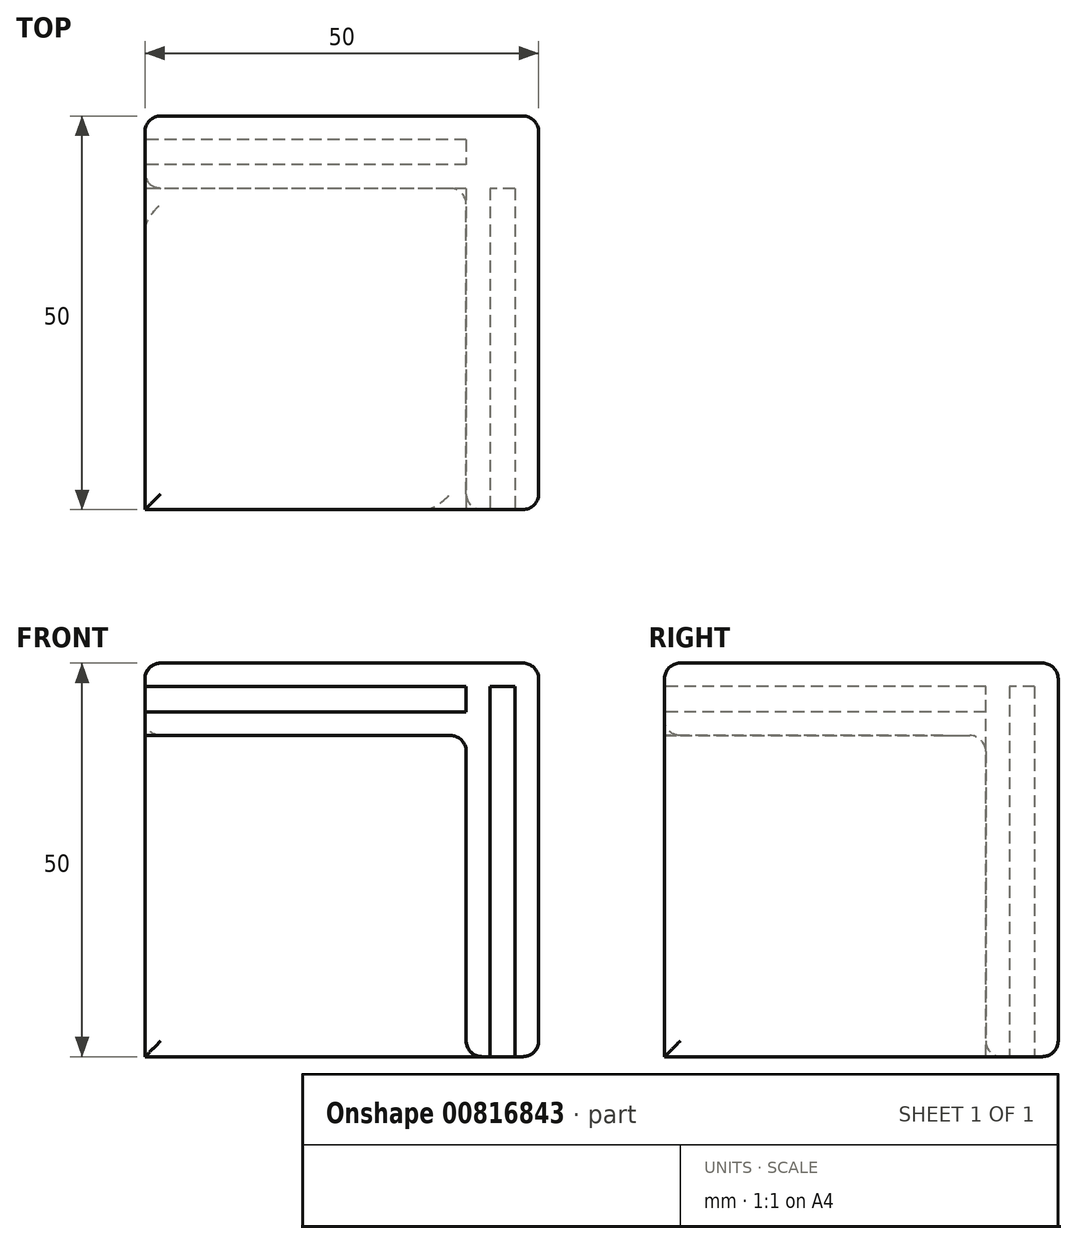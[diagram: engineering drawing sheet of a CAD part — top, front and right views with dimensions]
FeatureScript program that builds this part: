
annotation { "Feature Type Name" : "Feature", "Feature Type Description" : "" }
export const myFeature = defineFeature(function(context is Context, id is Id, definition is map)
    precondition{}
    {
        {
            var Q0;
            Q0=qCreatedBy(makeId("Top.planeOp"),FACE);
            var sketch = newSketch(context, id + "F0", { "sketchPlane" : qUnion([Q0])});
            skLineSegment(sketch, "E0.bottom", {"start": v(25, -25) * mm, "end": v(-25, -25) * mm});
            skLineSegment(sketch, "E0.top", {"start": v(25, 25) * mm, "end": v(-25, 25) * mm});
            skLineSegment(sketch, "E0.left", {"start": v(25, -25) * mm, "end": v(25, 25) * mm});
            skLineSegment(sketch, "E0.right", {"start": v(-25, -25) * mm, "end": v(-25, 25) * mm});
            skPoint(sketch, "E0.middle", {"position": v(0, 0) * mm});
            skSolve(sketch);
        }
        {
            var Q0;
            Q0=makeQuery(id+"F0.imprint","IMPRINT",FACE,{"disambiguationData":[TD([[makeQuery(id+"F0.imprint","IMPRINT",EDGE,{"derivedFrom":sQuery(id+"F0.wireOp",EDGE,"E0.bottom")}),-1.0]])]});
            extrude(context, id + "F1", {"entities" : qUnion([Q0]), "depth" : 3 * mm, "offsetDistance" : 25 * mm});
        }
        {
            var Q0;
            Q0=makeQuery(id+"F1.opExtrude","SWEPT_FACE",FACE,{"disambiguationData":[OSD([sQuery(id+"F0.wireOp",EDGE,"E0.right")])]});
            var sketch = newSketch(context, id + "F2", { "sketchPlane" : qUnion([Q0])});
            skLineSegment(sketch, "E1.bottom", {"start": v(-25, 3) * mm, "end": v(-22, 3) * mm});
            skLineSegment(sketch, "E1.top", {"start": v(-25, -47) * mm, "end": v(-22, -47) * mm});
            skLineSegment(sketch, "E1.left", {"start": v(-25, 3) * mm, "end": v(-25, -47) * mm});
            skLineSegment(sketch, "E1.right", {"start": v(-22, 3) * mm, "end": v(-22, -47) * mm});
            skLineSegment(sketch, "E2.bottom", {"start": v(-18.8, 3) * mm, "end": v(-15.8, 3) * mm});
            skLineSegment(sketch, "E2.top", {"start": v(-18.8, -47) * mm, "end": v(-15.8, -47) * mm});
            skLineSegment(sketch, "E2.left", {"start": v(-18.8, 3) * mm, "end": v(-18.8, -47) * mm});
            skLineSegment(sketch, "E2.right", {"start": v(-15.8, 3) * mm, "end": v(-15.8, -47) * mm});
            skSolve(sketch);
        }
        {
            var Q0;
            {var subQ0=sQuery(id+"F2.wireOp",EDGE,"E1.bottom");Q0=makeQuery(id+"F2.imprint","IMPRINT",FACE,{"disambiguationData":[TD([[makeQuery(id+"F2.imprint","IMPRINT",EDGE,{"derivedFrom":subQ0}),1.0]])]});}
            var Q1;
            {var subQ0=sQuery(id+"F2.wireOp",EDGE,"E2.bottom");Q1=makeQuery(id+"F2.imprint","IMPRINT",FACE,{"disambiguationData":[TD([[makeQuery(id+"F2.imprint","IMPRINT",EDGE,{"derivedFrom":subQ0}),1.0]])]});}
            var Q2;
            {var subQ0=sQuery(id+"F2.wireOp",EDGE,"E2.top");Q2=makeQuery(id+"F2.imprint","IMPRINT",FACE,{"disambiguationData":[TD([[makeQuery(id+"F2.imprint","IMPRINT",EDGE,{"derivedFrom":subQ0}),1.0]])]});}
            var Q3;
            {var subQ0=sQuery(id+"F2.wireOp",EDGE,"E1.top");Q3=makeQuery(id+"F2.imprint","IMPRINT",FACE,{"disambiguationData":[TD([[makeQuery(id+"F2.imprint","IMPRINT",EDGE,{"derivedFrom":subQ0}),1.0]])]});}
            var Q4;
            Q4=makeQuery(id+"F1.opExtrude","SWEPT_FACE",FACE,{"disambiguationData":[OSD([sQuery(id+"F0.wireOp",EDGE,"E0.left")])]});
            extrude(context, id + "F3", {"entities" : qUnion([Q0, Q1, Q2, Q3]), "operationType" : NewBodyOperationType.ADD, "endBound" : BoundingType.UP_TO_SURFACE, "oppositeDirection" : true, "depth" : 25 * mm, "endBoundEntityFace" : qUnion([Q4]), "offsetDistance" : 25 * mm});
        }
        {
            var Q0;
            Q0=makeQuery(id+"F1.opExtrude","SWEPT_FACE",FACE,{"disambiguationData":[OSD([sQuery(id+"F0.wireOp",EDGE,"E0.bottom")])]});
            var sketch = newSketch(context, id + "F4", { "sketchPlane" : qUnion([Q0])});
            skLineSegment(sketch, "E3.bottom", {"start": v(25, 3) * mm, "end": v(22, 3) * mm});
            skLineSegment(sketch, "E3.top", {"start": v(25, -47) * mm, "end": v(22, -47) * mm});
            skLineSegment(sketch, "E3.left", {"start": v(25, 3) * mm, "end": v(25, -47) * mm});
            skLineSegment(sketch, "E3.right", {"start": v(22, 3) * mm, "end": v(22, -47) * mm});
            skLineSegment(sketch, "E4.bottom", {"start": v(18.8, 3) * mm, "end": v(15.8, 3) * mm});
            skLineSegment(sketch, "E4.top", {"start": v(18.8, -47) * mm, "end": v(15.8, -47) * mm});
            skLineSegment(sketch, "E4.left", {"start": v(18.8, 3) * mm, "end": v(18.8, -47) * mm});
            skLineSegment(sketch, "E4.right", {"start": v(15.8, 3) * mm, "end": v(15.8, -47) * mm});
            skSolve(sketch);
        }
        {
            var Q0;
            Q0=qSketchRegion(id+"F4",true);
            var Q1;
            Q1=makeQuery(id+"F3.opExtrude","SWEPT_FACE",FACE,{"disambiguationData":[OSD([sQuery(id+"F2.wireOp",EDGE,"E1.right")])]});
            extrude(context, id + "F5", {"entities" : qUnion([Q0]), "operationType" : NewBodyOperationType.ADD, "endBound" : BoundingType.UP_TO_SURFACE, "oppositeDirection" : true, "depth" : 25 * mm, "endBoundEntityFace" : qUnion([Q1]), "offsetDistance" : 25 * mm});
        }
        {
            var Q0;
            {var subQ0=sQuery(id+"F2.wireOp",EDGE,"E1.right");var subQ1=makeQuery(id+"F3.opExtrude","SWEPT_FACE",FACE,{"disambiguationData":[OSD([subQ0])]});var subQ7=sQuery(id+"F0.wireOp",EDGE,"E0.right");var subQ8=sQuery(id+"F0.wireOp",EDGE,"E0.left");Q0=makeQuery(id+"F5.boolean.opBoolean","SPLIT",FACE,{"disambiguationData":[TD([makeQuery(id+"F5.opExtrude","SWEPT_FACE",FACE,{"disambiguationData":[OSD([sQuery(id+"F4.wireOp",EDGE,"E3.right")])]})])],"derivedFrom":makeQuery(id+"F3.boolean.opBoolean","SPLIT",FACE,{"disambiguationData":[TD([subQ1])],"derivedFrom":makeQuery(id+"F1.opExtrude","CAP_FACE",FACE,{"disambiguationData":[OSD([sQuery(id+"F0.wireOp",EDGE,"E0.bottom"),sQuery(id+"F0.wireOp",EDGE,"E0.top"),subQ8,subQ7])],"isStart":true})})});}
            var Q1;
            Q1=makeQuery(id+"F1.opExtrude","CAP_FACE",FACE,{"disambiguationData":[OSD([sQuery(id+"F0.wireOp",EDGE,"E0.bottom"),sQuery(id+"F0.wireOp",EDGE,"E0.top"),sQuery(id+"F0.wireOp",EDGE,"E0.left"),sQuery(id+"F0.wireOp",EDGE,"E0.right")])],"isStart":false});
            extrude(context, id + "F6", {"entities" : qUnion([Q0]), "operationType" : NewBodyOperationType.ADD, "endBound" : BoundingType.UP_TO_SURFACE, "oppositeDirection" : true, "depth" : 25 * mm, "endBoundEntityFace" : qUnion([Q1]), "offsetDistance" : 25 * mm});
        }
        {
            var Q0;
            Q0=makeQuery(id+"F5.boolean.opBoolean","MERGE",FACE,{"derivedFrom":[makeQuery(id+"F3.opExtrude","SWEPT_FACE",FACE,{"disambiguationData":[OSD([sQuery(id+"F2.wireOp",EDGE,"E1.top")])]}),makeQuery(id+"F3.opExtrude","SWEPT_FACE",FACE,{"disambiguationData":[OSD([sQuery(id+"F2.wireOp",EDGE,"E2.top")])]}),makeQuery(id+"F5.opExtrude","SWEPT_FACE",FACE,{"disambiguationData":[OSD([sQuery(id+"F4.wireOp",EDGE,"E3.top")])]}),makeQuery(id+"F5.opExtrude","SWEPT_FACE",FACE,{"disambiguationData":[OSD([sQuery(id+"F4.wireOp",EDGE,"E4.top")])]})]});
            var sketch = newSketch(context, id + "F7", { "sketchPlane" : qUnion([Q0])});
            skLineSegment(sketch, "E5.bottom", {"start": v(22, -18.8) * mm, "end": v(18.8, -18.8) * mm});
            skLineSegment(sketch, "E5.top", {"start": v(22, -22) * mm, "end": v(18.8, -22) * mm});
            skLineSegment(sketch, "E5.left", {"start": v(22, -18.8) * mm, "end": v(22, -22) * mm});
            skLineSegment(sketch, "E5.right", {"start": v(18.8, -18.8) * mm, "end": v(18.8, -22) * mm});
            skSolve(sketch);
        }
        {
            var Q0;
            Q0=qSketchRegion(id+"F7",true);
            var Q1;
            Q1=makeQuery(id+"F1.opExtrude","CAP_FACE",FACE,{"disambiguationData":[OSD([sQuery(id+"F0.wireOp",EDGE,"E0.bottom"),sQuery(id+"F0.wireOp",EDGE,"E0.top"),sQuery(id+"F0.wireOp",EDGE,"E0.left"),sQuery(id+"F0.wireOp",EDGE,"E0.right")])],"isStart":false});
            extrude(context, id + "F8", {"entities" : qUnion([Q0]), "operationType" : NewBodyOperationType.ADD, "endBound" : BoundingType.UP_TO_SURFACE, "oppositeDirection" : true, "depth" : 25 * mm, "endBoundEntityFace" : qUnion([Q1]), "offsetDistance" : 25 * mm});
        }
        {
            var Q0;
            Q0=makeQuery(id+"F3.boolean.opBoolean","MERGE",FACE,{"derivedFrom":[makeQuery(id+"F1.opExtrude","SWEPT_FACE",FACE,{"disambiguationData":[OSD([sQuery(id+"F0.wireOp",EDGE,"E0.right")])]}),makeQuery(id+"F3.opExtrude","CAP_FACE",FACE,{"disambiguationData":[OSD([sQuery(id+"F2.wireOp",EDGE,"E1.bottom"),sQuery(id+"F2.wireOp",EDGE,"E1.top"),sQuery(id+"F2.wireOp",EDGE,"E1.left"),sQuery(id+"F2.wireOp",EDGE,"E1.right")])],"isStart":true}),makeQuery(id+"F3.opExtrude","CAP_FACE",FACE,{"disambiguationData":[OSD([sQuery(id+"F2.wireOp",EDGE,"E2.bottom"),sQuery(id+"F2.wireOp",EDGE,"E2.top"),sQuery(id+"F2.wireOp",EDGE,"E2.left"),sQuery(id+"F2.wireOp",EDGE,"E2.right")])],"isStart":true})]});
            var sketch = newSketch(context, id + "F9", { "sketchPlane" : qUnion([Q0])});
            skLineSegment(sketch, "E6.bottom", {"start": v(-15.8, -3.2) * mm, "end": v(25, -3.2) * mm});
            skLineSegment(sketch, "E6.top", {"start": v(-15.8, -6.2) * mm, "end": v(25, -6.2) * mm});
            skLineSegment(sketch, "E6.left", {"start": v(-15.8, -3.2) * mm, "end": v(-15.8, -6.2) * mm});
            skLineSegment(sketch, "E6.right", {"start": v(25, -3.2) * mm, "end": v(25, -6.2) * mm});
            skLineSegment(sketch, "E7.0", {"start": v(25, 0) * mm, "end": v(25, -47) * mm});
            skSolve(sketch);
        }
        {
            var Q0;
            {var subQ0=sQuery(id+"F9.wireOp",EDGE,"E6.bottom");Q0=makeQuery(id+"F9.imprint","IMPRINT",FACE,{"disambiguationData":[TD([[makeQuery(id+"F9.imprint","IMPRINT",EDGE,{"derivedFrom":subQ0}),-1.0]])]});}
            var Q1;
            {var subQ1=sQuery(id+"F0.wireOp",EDGE,"E0.bottom");var subQ3=sQuery(id+"F4.wireOp",EDGE,"E4.right");Q1=makeQuery(id+"F5.boolean.opBoolean","SPLIT",FACE,{"disambiguationData":[TD([makeQuery(id+"F1.opExtrude","SWEPT_FACE",FACE,{"disambiguationData":[OSD([subQ1])]})])],"derivedFrom":makeQuery(id+"F5.opExtrude","SWEPT_FACE",FACE,{"disambiguationData":[OSD([subQ3])]})});}
            extrude(context, id + "F10", {"entities" : qUnion([Q0]), "operationType" : NewBodyOperationType.ADD, "endBound" : BoundingType.UP_TO_SURFACE, "oppositeDirection" : true, "depth" : 25 * mm, "endBoundEntityFace" : qUnion([Q1]), "offsetDistance" : 25 * mm});
        }
        {
            var Q0;
            Q0=makeQuery(id+"F1.opExtrude","CAP_EDGE",EDGE,{"disambiguationData":[OSD([sQuery(id+"F0.wireOp",EDGE,"E0.right")])],"isStart":false});
            var Q1;
            Q1=makeQuery(id+"F1.opExtrude","CAP_EDGE",EDGE,{"disambiguationData":[OSD([sQuery(id+"F0.wireOp",EDGE,"E0.bottom")])],"isStart":false});
            var Q2;
            Q2=makeQuery(id+"F1.opExtrude","CAP_EDGE",EDGE,{"disambiguationData":[OSD([sQuery(id+"F0.wireOp",EDGE,"E0.top")])],"isStart":false});
            var Q3;
            Q3=makeQuery(id+"F1.opExtrude","CAP_EDGE",EDGE,{"disambiguationData":[OSD([sQuery(id+"F0.wireOp",EDGE,"E0.left")])],"isStart":false});
            var Q4;
            Q4=makeQuery(id+"F5.boolean.opBoolean","MERGE",FACE,{"derivedFrom":[makeQuery(id+"F3.boolean.opBoolean","MERGE",FACE,{"derivedFrom":[makeQuery(id+"F1.opExtrude","SWEPT_FACE",FACE,{"disambiguationData":[OSD([sQuery(id+"F0.wireOp",EDGE,"E0.left")])]}),makeQuery(id+"F3.opExtrude","CAP_FACE",FACE,{"disambiguationData":[OSD([sQuery(id+"F2.wireOp",EDGE,"E1.bottom"),sQuery(id+"F2.wireOp",EDGE,"E1.top"),sQuery(id+"F2.wireOp",EDGE,"E1.left"),sQuery(id+"F2.wireOp",EDGE,"E1.right")])],"isStart":false}),makeQuery(id+"F3.opExtrude","CAP_FACE",FACE,{"disambiguationData":[OSD([sQuery(id+"F2.wireOp",EDGE,"E2.bottom"),sQuery(id+"F2.wireOp",EDGE,"E2.top"),sQuery(id+"F2.wireOp",EDGE,"E2.left"),sQuery(id+"F2.wireOp",EDGE,"E2.right")])],"isStart":false})]}),makeQuery(id+"F5.opExtrude","SWEPT_FACE",FACE,{"disambiguationData":[OSD([sQuery(id+"F4.wireOp",EDGE,"E3.left")])]})]});
            var Q5;
            Q5=makeQuery(id+"F3.boolean.opBoolean","MERGE",FACE,{"derivedFrom":[makeQuery(id+"F1.opExtrude","SWEPT_FACE",FACE,{"disambiguationData":[OSD([sQuery(id+"F0.wireOp",EDGE,"E0.top")])]}),makeQuery(id+"F3.opExtrude","SWEPT_FACE",FACE,{"disambiguationData":[OSD([sQuery(id+"F2.wireOp",EDGE,"E1.left")])]})]});
            var Q6;
            {var subQ1=sQuery(id+"F4.wireOp",EDGE,"E4.right");var subQ7=sQuery(id+"F0.wireOp",EDGE,"E0.bottom");var subQ8=makeQuery(id+"F1.opExtrude","SWEPT_FACE",FACE,{"disambiguationData":[OSD([subQ7])]});var subQ10=makeQuery(id+"F3.opExtrude","SWEPT_FACE",FACE,{"disambiguationData":[OSD([sQuery(id+"F2.wireOp",EDGE,"E1.top")])]});Q6=makeQuery(id+"F10.boolean.opBoolean","SPLIT",FACE,{"disambiguationData":[TD([subQ10])],"derivedFrom":makeQuery(id+"F5.boolean.opBoolean","SPLIT",FACE,{"disambiguationData":[TD([subQ8])],"derivedFrom":makeQuery(id+"F5.opExtrude","SWEPT_FACE",FACE,{"disambiguationData":[OSD([subQ1])]})})});}
            var Q7;
            {var subQ1=sQuery(id+"F2.wireOp",EDGE,"E2.right");var subQ5=sQuery(id+"F0.wireOp",EDGE,"E0.right");var subQ6=makeQuery(id+"F1.opExtrude","SWEPT_FACE",FACE,{"disambiguationData":[OSD([subQ5])]});var subQ7=sQuery(id+"F2.wireOp",EDGE,"E1.top");var subQ12=makeQuery(id+"F3.opExtrude","SWEPT_FACE",FACE,{"disambiguationData":[OSD([subQ7])]});Q7=makeQuery(id+"F10.boolean.opBoolean","SPLIT",FACE,{"disambiguationData":[TD([subQ12])],"derivedFrom":makeQuery(id+"F5.boolean.opBoolean","SPLIT",FACE,{"disambiguationData":[TD([subQ6])],"derivedFrom":makeQuery(id+"F3.opExtrude","SWEPT_FACE",FACE,{"disambiguationData":[OSD([subQ1])]})})});}
            fillet(context, id + "F11", {"entities" : qUnion([Q0, Q1, Q2, Q3, Q4, Q5, Q6, Q7]), "radius" : 2 * mm, "tangentPropagation" : true, "allowEdgeOverflow" : false});
        }
    });
